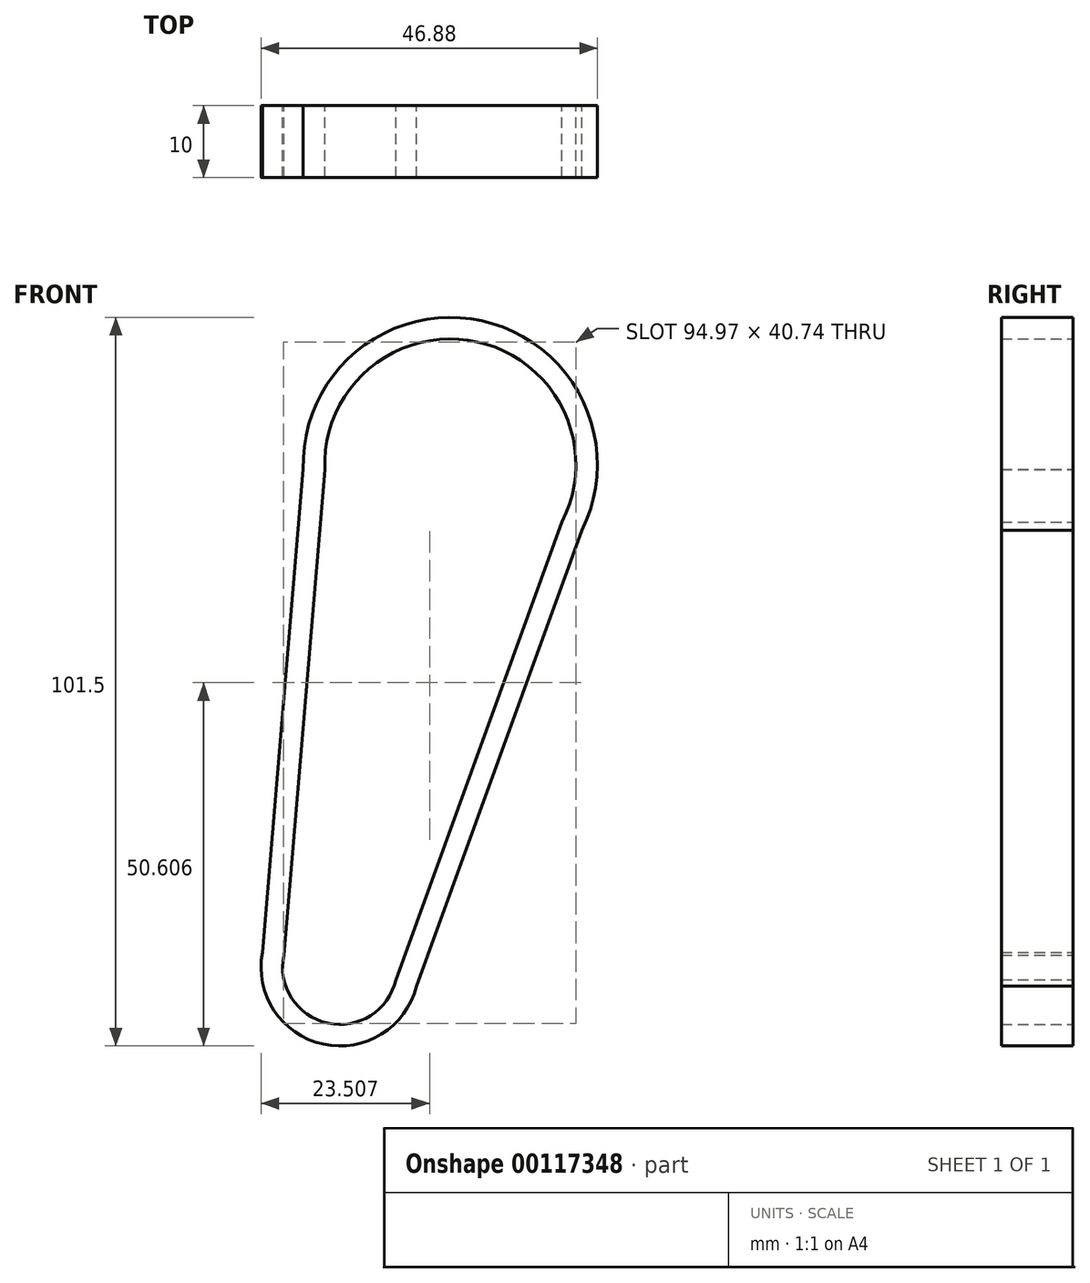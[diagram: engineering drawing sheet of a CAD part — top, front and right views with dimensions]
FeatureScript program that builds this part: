
annotation { "Feature Type Name" : "Feature", "Feature Type Description" : "" }
export const myFeature = defineFeature(function(context is Context, id is Id, definition is map)
    precondition{}
    {
        {
            var Q0;
            Q0=qCreatedBy(makeId("Front.planeOp"),FACE);
            var sketch = newSketch(context, id + "F0", { "sketchPlane" : qUnion([Q0])});
            skArc(sketch, "E0", {"start": v(-7.83, 1.63) * mm, "mid": v(-1.72, -7.81) * mm, "end": v(7.8, -1.8) * mm});
            skArc(sketch, "E1", {"start": v(30.95, 62.01) * mm, "mid": v(19.14, 87.1) * mm, "end": v(-2.1, 69.28) * mm});
            skLineSegment(sketch, "E2", {"start": v(-2.1, 69.28) * mm, "end": v(-7.83, 1.63) * mm});
            skLineSegment(sketch, "E3", {"start": v(30.95, 62.01) * mm, "end": v(7.8, -1.8) * mm});
            skArc(sketch, "E4.0", {"start": v(33.71, 60.82) * mm, "mid": v(19.78, 90.02) * mm, "end": v(-5.1, 69.35) * mm});
            skLineSegment(sketch, "E4.1", {"start": v(33.71, 60.82) * mm, "end": v(10.67, -2.67) * mm});
            skArc(sketch, "E4.2", {"start": v(-10.8, 2.05) * mm, "mid": v(-2.36, -10.74) * mm, "end": v(10.67, -2.67) * mm});
            skLineSegment(sketch, "E4.3", {"start": v(-5.1, 69.35) * mm, "end": v(-10.8, 2.05) * mm});
            skSolve(sketch);
        }
        {
            var Q0;
            Q0 = qSketchRegion(id + "F0", true);
            extrude(context, id + "F1", {"entities" : qUnion([Q0]), "depth" : 10 * mm});
        }
    });
